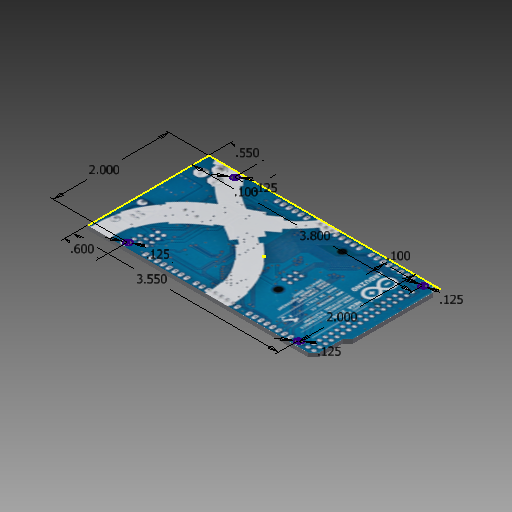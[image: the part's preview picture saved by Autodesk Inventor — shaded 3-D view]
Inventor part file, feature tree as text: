
AUTODESK INVENTOR PART (.ipt)
format: ipt  version: 2018 (Build 220112000, 112)  size: 465,408 bytes
history: native  units: in
note: dims shown in document units (in); Inventor stores cm internally (conversion verified against a paired STEP export)
features: sketch x5, other x4, extrude x3, chamfer x2
ambient origin geometry x8: Origin, YZ Plane, XZ Plane, XY Plane, X Axis, Y Axis, Z Axis, Center Point
bodies: Solid1 (feature_tree)
feature tree (14):
  extrude  "Extrusion1"  Depth=2.095in
  extrude  "Extrusion2"  Depth=0.065in
  chamfer  "Chamfer1"  Distance=0.125in
  other  "Decal1"
  extrude  "Extrusion3"  Depth=0.065in
  chamfer  "Chamfer2"  Distance=0.065in
  other  "Decal2"
  sketch  "Sketch1"  dims[d0=4.0in d1=2.095in]
  sketch  "Sketch3"  dims[d2=0.065in d3=0.0in d4=0.125in]
  sketch  "Sketch5"  dims[d5=0.1in]
  other  "Image1"
  sketch  "Sketch6"  dims[d6=0.55in]
  sketch  "Sketch7"  dims[d7=0.125in d10=0.125in d12=0.125in d16=0.065in d17=0.0in d18=0.125in d19=0.125in d20=45.0deg d25=0.065in d26=0.0in d27=0.09in d28=0.125in d29=45.0deg d35=2.0in d36=0.6in d37=0.1in d38=3.8in d39=2.0in d40=3.55in]
  other  "Image2"
